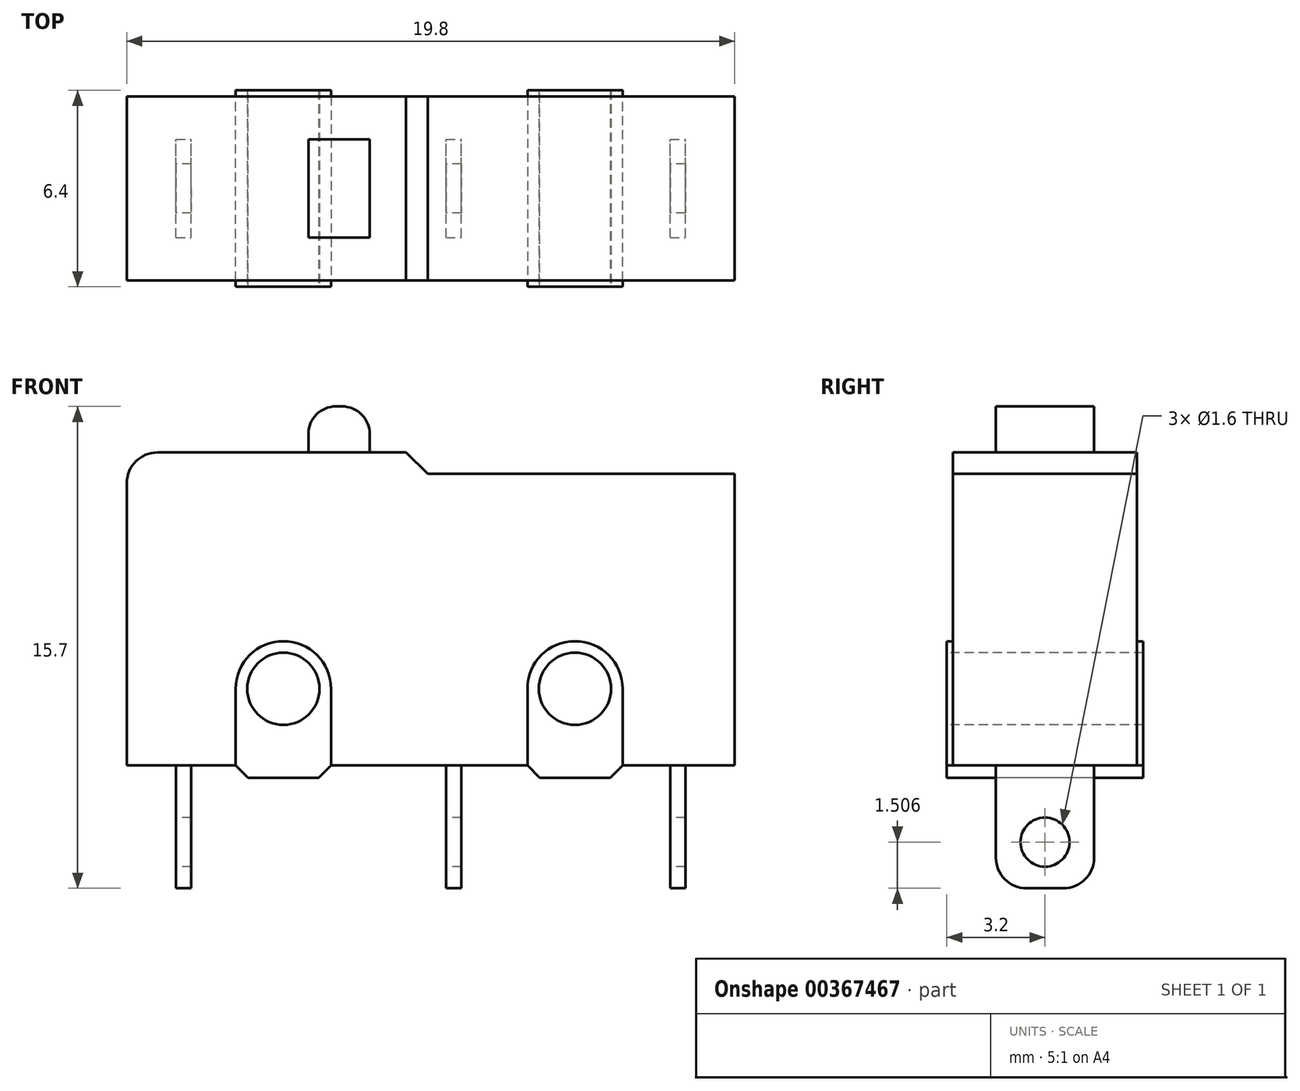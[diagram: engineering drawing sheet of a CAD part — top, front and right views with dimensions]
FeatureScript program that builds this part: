
annotation { "Feature Type Name" : "Feature", "Feature Type Description" : "" }
export const myFeature = defineFeature(function(context is Context, id is Id, definition is map)
    precondition{}
    {
        {
            var Q0;
            Q0=qCreatedBy(makeId("Front.planeOp"),FACE);
            var sketch = newSketch(context, id + "F0", { "sketchPlane" : qUnion([Q0])});
            skLineSegment(sketch, "E0.bottom", {"start": v(0, 0) * mm, "end": v(19.8, 0) * mm});
            skLineSegment(sketch, "E0.top", {"start": v(0, 10.2) * mm, "end": v(19.8, 10.2) * mm});
            skLineSegment(sketch, "E0.left", {"start": v(0, 0) * mm, "end": v(0, 10.2) * mm});
            skLineSegment(sketch, "E0.right", {"start": v(19.8, 0) * mm, "end": v(19.8, 10.2) * mm});
            skSolve(sketch);
        }
        {
            var Q0;
            Q0=qSketchRegion(id+"F0",true);
            extrude(context, id + "F1", {"entities" : qUnion([Q0]), "depth" : 6 * mm});
        }
        {
            var Q0;
            Q0=makeQuery(id+"F1.opExtrude","CAP_FACE",FACE,{"disambiguationData":[OSD([sQuery(id+"F0.wireOp",EDGE,"E0.bottom"),sQuery(id+"F0.wireOp",EDGE,"E0.top"),sQuery(id+"F0.wireOp",EDGE,"E0.left"),sQuery(id+"F0.wireOp",EDGE,"E0.right")])],"isStart":false});
            var sketch = newSketch(context, id + "F2", { "sketchPlane" : qUnion([Q0])});
            skLineSegment(sketch, "E1", {"start": v(0, 2.5) * mm, "end": v(19.8, 2.5) * mm, "construction": true});
            skCircle(sketch, "E2", {"center": v(5.1, 2.5) * mm, "radius": 1.55 * mm});
            skCircle(sketch, "E3", {"center": v(14.6, 2.5) * mm, "radius": 1.55 * mm});
            skLineSegment(sketch, "E4", {"start": v(6.65, 2.5) * mm, "end": v(6.65, -0.4) * mm});
            skLineSegment(sketch, "E5", {"start": v(6.65, -0.4) * mm, "end": v(3.55, -0.4) * mm});
            skLineSegment(sketch, "E6", {"start": v(3.55, -0.4) * mm, "end": v(3.55, 2.5) * mm});
            skLineSegment(sketch, "E7", {"start": v(13.05, 2.5) * mm, "end": v(13.05, -0.4) * mm});
            skLineSegment(sketch, "E8", {"start": v(13.05, -0.4) * mm, "end": v(16.15, -0.4) * mm});
            skLineSegment(sketch, "E9", {"start": v(16.15, -0.4) * mm, "end": v(16.15, 2.5) * mm});
            skSolve(sketch);
        }
        {
            var Q0;
            Q0=qSketchRegion(id+"F2",true);
            extrude(context, id + "F3", {"entities" : qUnion([Q0]), "operationType" : NewBodyOperationType.ADD, "depth" : 0.2 * mm});
        }
        {
            var Q0;
            Q0=makeQuery(id+"F3.opExtrude","CAP_FACE",FACE,{"disambiguationData":[OSD([sQuery(id+"F2.wireOp",EDGE,"E2"),sQuery(id+"F2.wireOp",EDGE,"E4"),sQuery(id+"F2.wireOp",EDGE,"E5"),sQuery(id+"F2.wireOp",EDGE,"E6")])],"isStart":false});
            var sketch = newSketch(context, id + "F4", { "sketchPlane" : qUnion([Q0])});
            skSolve(sketch);
        }
        {
            var Q0;
            Q0=qSketchRegion(id+"F4",true);
            var Q1;
            Q1=makeQuery(id+"F4.imprint","IMPRINT",FACE,{"disambiguationData":[TD([[makeQuery(id+"F4.imprint","IMPRINT",EDGE,{"derivedFrom":makeQuery(id+"F3.opExtrude","CAP_EDGE",EDGE,{"disambiguationData":[OSD([sQuery(id+"F2.wireOp",EDGE,"E2")])],"isStart":false})}),1.0]])]});
            extrude(context, id + "F5", {"entities" : qUnion([Q0, Q1]), "operationType" : NewBodyOperationType.ADD, "oppositeDirection" : true, "depth" : 6.4 * mm});
        }
        {
            var Q0;
            Q0=makeQuery(id+"F3.opExtrude","CAP_FACE",FACE,{"disambiguationData":[OSD([sQuery(id+"F2.wireOp",EDGE,"E3"),sQuery(id+"F2.wireOp",EDGE,"E7"),sQuery(id+"F2.wireOp",EDGE,"E8"),sQuery(id+"F2.wireOp",EDGE,"E9")])],"isStart":false});
            extrude(context, id + "F6", {"entities" : qUnion([Q0]), "operationType" : NewBodyOperationType.ADD, "oppositeDirection" : true, "depth" : 6.4 * mm});
        }
        {
            var Q0;
            {var subQ0=sQuery(id+"F2.wireOp",EDGE,"E6");var subQ1=sQuery(id+"F2.wireOp",EDGE,"E5");Q0=makeQuery(id+"F5.boolean.opBoolean","MERGE",EDGE,{"derivedFrom":[makeQuery(id+"F3.opExtrude","SWEPT_EDGE",EDGE,{"disambiguationData":[OSD([subQ1,subQ0])]}),makeQuery(id+"F5.opExtrude","SWEPT_EDGE",EDGE,{"disambiguationData":[OSD([subQ1,subQ0])]})]});}
            var Q1;
            {var subQ0=sQuery(id+"F2.wireOp",EDGE,"E5");var subQ1=sQuery(id+"F2.wireOp",EDGE,"E4");Q1=makeQuery(id+"F5.boolean.opBoolean","MERGE",EDGE,{"derivedFrom":[makeQuery(id+"F3.opExtrude","SWEPT_EDGE",EDGE,{"disambiguationData":[OSD([subQ1,subQ0])]}),makeQuery(id+"F5.opExtrude","SWEPT_EDGE",EDGE,{"disambiguationData":[OSD([subQ1,subQ0])]})]});}
            var Q2;
            {var subQ0=sQuery(id+"F2.wireOp",EDGE,"E8");var subQ1=sQuery(id+"F2.wireOp",EDGE,"E7");Q2=makeQuery(id+"F6.boolean.opBoolean","MERGE",EDGE,{"derivedFrom":[makeQuery(id+"F3.opExtrude","SWEPT_EDGE",EDGE,{"disambiguationData":[OSD([subQ1,subQ0])]}),makeQuery(id+"F6.opExtrude","SWEPT_EDGE",EDGE,{"disambiguationData":[OSD([subQ1,subQ0])]})]});}
            var Q3;
            {var subQ0=sQuery(id+"F2.wireOp",EDGE,"E9");var subQ1=sQuery(id+"F2.wireOp",EDGE,"E8");Q3=makeQuery(id+"F6.boolean.opBoolean","MERGE",EDGE,{"derivedFrom":[makeQuery(id+"F3.opExtrude","SWEPT_EDGE",EDGE,{"disambiguationData":[OSD([subQ1,subQ0])]}),makeQuery(id+"F6.opExtrude","SWEPT_EDGE",EDGE,{"disambiguationData":[OSD([subQ1,subQ0])]})]});}
            chamfer(context, id + "F7", {"entities" : qUnion([Q0, Q1, Q2, Q3]), "width" : 0.4 * mm, "tangentPropagation" : true});
        }
        {
            var Q0;
            Q0=makeQuery(id+"F1.opExtrude","CAP_FACE",FACE,{"disambiguationData":[OSD([sQuery(id+"F0.wireOp",EDGE,"E0.bottom"),sQuery(id+"F0.wireOp",EDGE,"E0.top"),sQuery(id+"F0.wireOp",EDGE,"E0.left"),sQuery(id+"F0.wireOp",EDGE,"E0.right")])],"isStart":false});
            var sketch = newSketch(context, id + "F8", { "sketchPlane" : qUnion([Q0])});
            skLineSegment(sketch, "E10", {"start": v(9.1, 10.2) * mm, "end": v(9.8, 9.5) * mm});
            skLineSegment(sketch, "E11", {"start": v(9.8, 9.5) * mm, "end": v(19.8, 9.5) * mm});
            skLineSegment(sketch, "E12", {"start": v(19.8, 9.5) * mm, "end": v(19.8, 10.2) * mm});
            skLineSegment(sketch, "E13", {"start": v(19.8, 10.2) * mm, "end": v(9.1, 10.2) * mm});
            skSolve(sketch);
        }
        {
            var Q0;
            Q0=qSketchRegion(id+"F8",true);
            extrude(context, id + "F9", {"entities" : qUnion([Q0]), "operationType" : NewBodyOperationType.REMOVE, "endBound" : BoundingType.THROUGH_ALL, "oppositeDirection" : true, "depth" : 25 * mm});
        }
        {
            var Q0;
            Q0=makeQuery(id+"F1.opExtrude","SWEPT_EDGE",EDGE,{"disambiguationData":[OSD([sQuery(id+"F0.wireOp",EDGE,"E0.top"),sQuery(id+"F0.wireOp",EDGE,"E0.left")])]});
            var Q1;
            Q1=makeQuery(id+"F9.boolean.opBoolean","COPY",EDGE,{"derivedFrom":makeQuery(id+"F9.opExtrude","SWEPT_EDGE",EDGE,{"disambiguationData":[OSD([sQuery(id+"F0.wireOp",EDGE,"E0.right"),sQuery(id+"F8.wireOp",EDGE,"E11"),sQuery(id+"F8.wireOp",EDGE,"E12")])]})});
            fillet(context, id + "F10", {"entities" : qUnion([Q0, Q1]), "radius" : 1 * mm, "tangentPropagation" : true, "allowEdgeOverflow" : false});
        }
        {
            var Q0;
            Q0=makeQuery(id+"F3.opExtrude","CAP_FACE",FACE,{"disambiguationData":[OSD([sQuery(id+"F2.wireOp",EDGE,"E2"),sQuery(id+"F2.wireOp",EDGE,"E4"),sQuery(id+"F2.wireOp",EDGE,"E5"),sQuery(id+"F2.wireOp",EDGE,"E6")])],"isStart":false});
            var sketch = newSketch(context, id + "F11", { "sketchPlane" : qUnion([Q0])});
            skLineSegment(sketch, "E14", {"start": v(0, 2.5) * mm, "end": v(17.98, 2.5) * mm, "construction": true});
            skPoint(sketch, "E15", {"position": v(5.1, 2.5) * mm});
            skSolve(sketch);
        }
        {
            var Q0;
            Q0=sQuery(id+"F11.wireOp",VERTEX,"E15");
            var Q1;
            Q1=makeQuery(id+"F1.opExtrude","SWEPT_BODY",BODY,{"disambiguationData":[OSD([sQuery(id+"F0.wireOp",EDGE,"E0.bottom"),sQuery(id+"F0.wireOp",EDGE,"E0.top"),sQuery(id+"F0.wireOp",EDGE,"E0.left"),sQuery(id+"F0.wireOp",EDGE,"E0.right")])]});
            hole(context, id + "F12", {"style" : HoleStyle.SIMPLE, "endStyle" : HoleEndStyle.THROUGH, "holeDiameter" : 2.35 * mm, "locations" : qUnion([Q0]), "scope" : qUnion([Q1]), "isTappedThrough" : true});
        }
        {
            var Q0;
            Q0=makeQuery(id+"F3.opExtrude","CAP_FACE",FACE,{"disambiguationData":[OSD([sQuery(id+"F2.wireOp",EDGE,"E3"),sQuery(id+"F2.wireOp",EDGE,"E7"),sQuery(id+"F2.wireOp",EDGE,"E8"),sQuery(id+"F2.wireOp",EDGE,"E9")])],"isStart":false});
            var sketch = newSketch(context, id + "F13", { "sketchPlane" : qUnion([Q0])});
            skLineSegment(sketch, "E16", {"start": v(16.15, 2.5) * mm, "end": v(10.83, 2.5) * mm, "construction": true});
            skPoint(sketch, "E17", {"position": v(14.6, 2.5) * mm});
            skSolve(sketch);
        }
        {
            var Q0;
            Q0=sQuery(id+"F13.wireOp",VERTEX,"E17");
            var Q1;
            Q1=makeQuery(id+"F1.opExtrude","SWEPT_BODY",BODY,{"disambiguationData":[OSD([sQuery(id+"F0.wireOp",EDGE,"E0.bottom"),sQuery(id+"F0.wireOp",EDGE,"E0.top"),sQuery(id+"F0.wireOp",EDGE,"E0.left"),sQuery(id+"F0.wireOp",EDGE,"E0.right")])]});
            hole(context, id + "F14", {"style" : HoleStyle.SIMPLE, "endStyle" : HoleEndStyle.THROUGH, "holeDiameter" : 2.35 * mm, "locations" : qUnion([Q0]), "scope" : qUnion([Q1]), "isTappedThrough" : true});
        }
        {
            var Q0;
            Q0=makeQuery(id+"F1.opExtrude","SWEPT_FACE",FACE,{"disambiguationData":[OSD([sQuery(id+"F0.wireOp",EDGE,"E0.top")])]});
            var sketch = newSketch(context, id + "F15", { "sketchPlane" : qUnion([Q0])});
            skLineSegment(sketch, "E18.bottom", {"start": v(5.91, -1.4) * mm, "end": v(7.91, -1.4) * mm});
            skLineSegment(sketch, "E18.top", {"start": v(5.91, -4.6) * mm, "end": v(7.91, -4.6) * mm});
            skLineSegment(sketch, "E18.left", {"start": v(5.91, -1.4) * mm, "end": v(5.91, -4.6) * mm});
            skLineSegment(sketch, "E18.right", {"start": v(7.91, -1.4) * mm, "end": v(7.91, -4.6) * mm});
            skLineSegment(sketch, "E19", {"start": v(5.91, -1.4) * mm, "end": v(5.91, 0) * mm, "construction": true});
            skLineSegment(sketch, "E20", {"start": v(5.91, -4.6) * mm, "end": v(5.91, -6) * mm, "construction": true});
            skSolve(sketch);
        }
        {
            var Q0;
            Q0=qSketchRegion(id+"F15",true);
            extrude(context, id + "F16", {"entities" : qUnion([Q0]), "operationType" : NewBodyOperationType.ADD, "depth" : 1.5 * mm});
        }
        {
            var Q0;
            Q0=makeQuery(id+"F16.opExtrude","CAP_EDGE",EDGE,{"disambiguationData":[OSD([sQuery(id+"F15.wireOp",EDGE,"E18.left")])],"isStart":false});
            var Q1;
            Q1=makeQuery(id+"F16.opExtrude","CAP_EDGE",EDGE,{"disambiguationData":[OSD([sQuery(id+"F15.wireOp",EDGE,"E18.right")])],"isStart":false});
            fillet(context, id + "F17", {"entities" : qUnion([Q0, Q1]), "radius" : 0.9 * mm, "tangentPropagation" : true, "allowEdgeOverflow" : false});
        }
        {
            var Q0;
            {var subQ0=sQuery(id+"F0.wireOp",EDGE,"E0.left");var subQ4=sQuery(id+"F0.wireOp",EDGE,"E0.bottom");Q0=makeQuery(id+"F5.boolean.opBoolean","SPLIT",FACE,{"disambiguationData":[TD([makeQuery(id+"F1.opExtrude","SWEPT_FACE",FACE,{"disambiguationData":[OSD([subQ0])]})])],"derivedFrom":makeQuery(id+"F1.opExtrude","SWEPT_FACE",FACE,{"disambiguationData":[OSD([subQ4])]})});}
            var sketch = newSketch(context, id + "F18", { "sketchPlane" : qUnion([Q0])});
            skLineSegment(sketch, "E21.bottom", {"start": v(1.6, 4.6) * mm, "end": v(2.1, 4.6) * mm});
            skLineSegment(sketch, "E21.top", {"start": v(1.6, 1.4) * mm, "end": v(2.1, 1.4) * mm});
            skLineSegment(sketch, "E21.left", {"start": v(1.6, 4.6) * mm, "end": v(1.6, 1.4) * mm});
            skLineSegment(sketch, "E21.right", {"start": v(2.1, 4.6) * mm, "end": v(2.1, 1.4) * mm});
            skLineSegment(sketch, "E22.bottom", {"start": v(10.4, 4.6) * mm, "end": v(10.9, 4.6) * mm});
            skLineSegment(sketch, "E22.top", {"start": v(10.4, 1.4) * mm, "end": v(10.9, 1.4) * mm});
            skLineSegment(sketch, "E22.left", {"start": v(10.4, 4.6) * mm, "end": v(10.4, 1.4) * mm});
            skLineSegment(sketch, "E22.right", {"start": v(10.9, 4.6) * mm, "end": v(10.9, 1.4) * mm});
            skLineSegment(sketch, "E23.bottom", {"start": v(17.7, 4.6) * mm, "end": v(18.2, 4.6) * mm});
            skLineSegment(sketch, "E23.top", {"start": v(17.7, 1.4) * mm, "end": v(18.2, 1.4) * mm});
            skLineSegment(sketch, "E23.left", {"start": v(17.7, 4.6) * mm, "end": v(17.7, 1.4) * mm});
            skLineSegment(sketch, "E23.right", {"start": v(18.2, 4.6) * mm, "end": v(18.2, 1.4) * mm});
            skPoint(sketch, "E24.end.orphan", {"position": v(1.6, 0) * mm});
            skPoint(sketch, "E25.end.orphan", {"position": v(10.4, 0) * mm});
            skPoint(sketch, "E26.end.orphan", {"position": v(17.7, 0) * mm});
            skSolve(sketch);
        }
        {
            var Q0;
            Q0=qSketchRegion(id+"F18",true);
            extrude(context, id + "F19", {"entities" : qUnion([Q0]), "operationType" : NewBodyOperationType.ADD, "depth" : 4 * mm});
        }
        {
            var Q0;
            Q0=makeQuery(id+"F19.opExtrude","SWEPT_FACE",FACE,{"disambiguationData":[OSD([sQuery(id+"F18.wireOp",EDGE,"E21.left")])]});
            var sketch = newSketch(context, id + "F20", { "sketchPlane" : qUnion([Q0])});
            skPoint(sketch, "E27", {"position": v(3, -2.5) * mm});
            skPoint(sketch, "E27.positionSnap0", {"position": v(3, -4) * mm});
            skSolve(sketch);
        }
        {
            var Q0;
            Q0=sQuery(id+"F20.wireOp",VERTEX,"E27");
            var Q1;
            Q1=makeQuery(id+"F1.opExtrude","SWEPT_BODY",BODY,{"disambiguationData":[OSD([sQuery(id+"F0.wireOp",EDGE,"E0.bottom"),sQuery(id+"F0.wireOp",EDGE,"E0.top"),sQuery(id+"F0.wireOp",EDGE,"E0.left"),sQuery(id+"F0.wireOp",EDGE,"E0.right")])]});
            hole(context, id + "F21", {"style" : HoleStyle.SIMPLE, "endStyle" : HoleEndStyle.THROUGH, "holeDiameter" : 1.6 * mm, "locations" : qUnion([Q0]), "scope" : qUnion([Q1]), "isTappedThrough" : true});
        }
        {
            var Q0;
            Q0=makeQuery(id+"F19.opExtrude","CAP_EDGE",EDGE,{"disambiguationData":[OSD([sQuery(id+"F18.wireOp",EDGE,"E23.bottom")])],"isStart":false});
            var Q1;
            Q1=makeQuery(id+"F19.opExtrude","CAP_EDGE",EDGE,{"disambiguationData":[OSD([sQuery(id+"F18.wireOp",EDGE,"E22.bottom")])],"isStart":false});
            var Q2;
            Q2=makeQuery(id+"F19.opExtrude","CAP_EDGE",EDGE,{"disambiguationData":[OSD([sQuery(id+"F18.wireOp",EDGE,"E21.bottom")])],"isStart":false});
            var Q3;
            Q3=makeQuery(id+"F19.opExtrude","CAP_EDGE",EDGE,{"disambiguationData":[OSD([sQuery(id+"F18.wireOp",EDGE,"E21.top")])],"isStart":false});
            var Q4;
            Q4=makeQuery(id+"F19.opExtrude","CAP_EDGE",EDGE,{"disambiguationData":[OSD([sQuery(id+"F18.wireOp",EDGE,"E22.top")])],"isStart":false});
            var Q5;
            Q5=makeQuery(id+"F19.opExtrude","CAP_EDGE",EDGE,{"disambiguationData":[OSD([sQuery(id+"F18.wireOp",EDGE,"E23.top")])],"isStart":false});
            fillet(context, id + "F22", {"entities" : qUnion([Q0, Q1, Q2, Q3, Q4, Q5]), "radius" : 1 * mm, "tangentPropagation" : true, "allowEdgeOverflow" : false});
        }
    });
